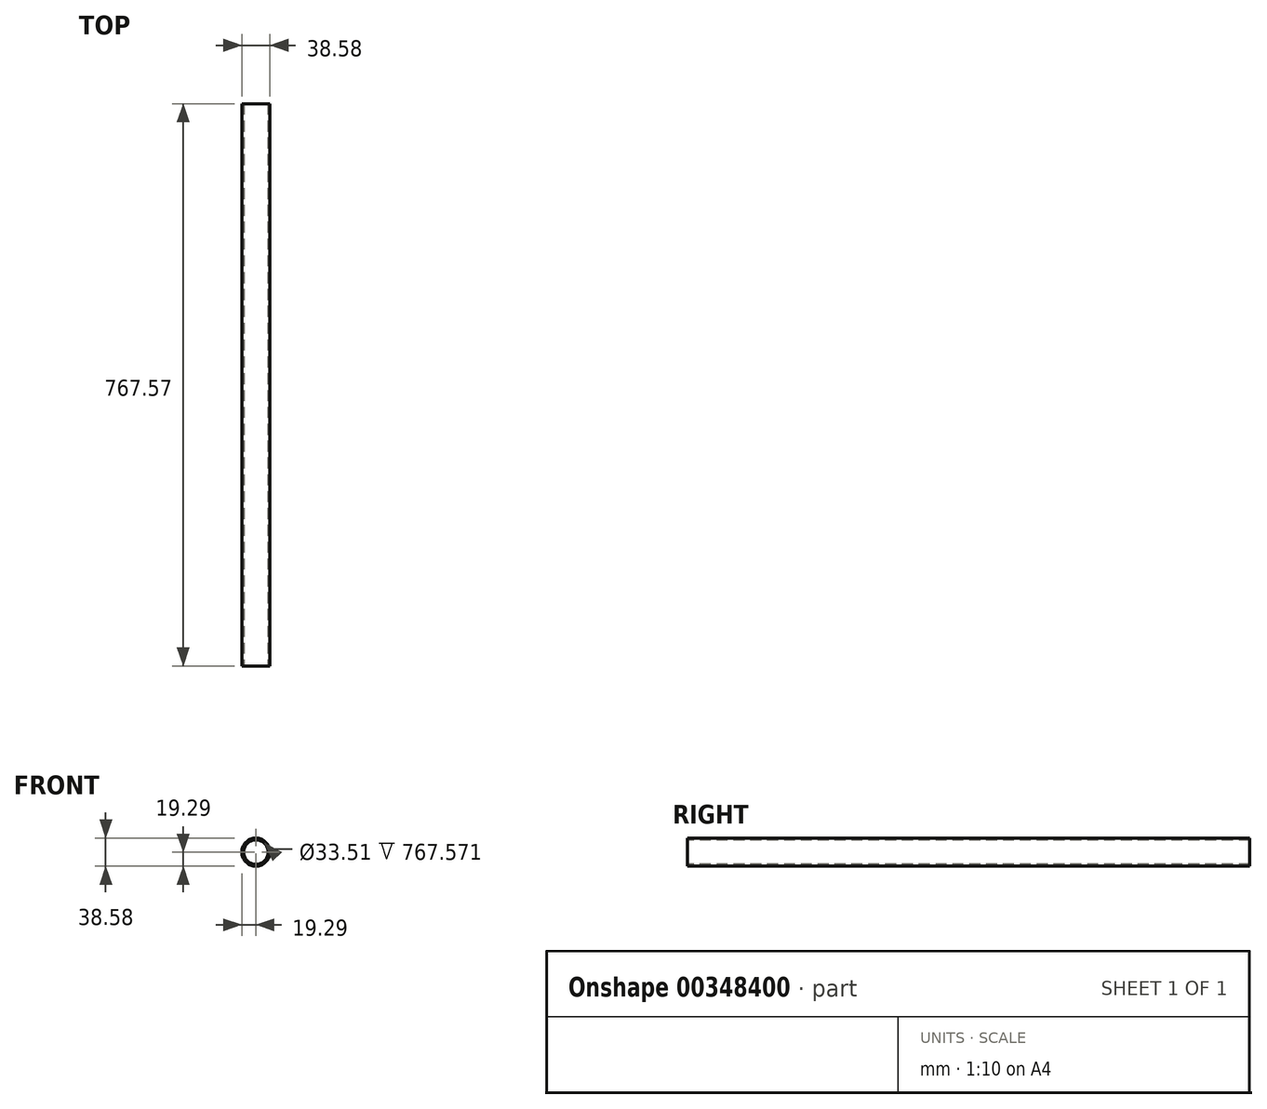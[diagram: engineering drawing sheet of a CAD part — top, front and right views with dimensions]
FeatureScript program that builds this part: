
annotation { "Feature Type Name" : "Feature", "Feature Type Description" : "" }
export const myFeature = defineFeature(function(context is Context, id is Id, definition is map)
    precondition{}
    {
        {
            var Q0;
            Q0=qCreatedBy(makeId("Front.planeOp"),FACE);
            var sketch = newSketch(context, id + "F0", { "sketchPlane" : qUnion([Q0])});
            skCircle(sketch, "E0", {"center": v(0, 0) * mm, "radius": 19.3 * mm});
            skSolve(sketch);
        }
        {
            var Q0;
            Q0=qCreatedBy(makeId("Top.planeOp"),FACE);
            var sketch = newSketch(context, id + "F1", { "sketchPlane" : qUnion([Q0])});
            skLineSegment(sketch, "E1", {"start": v(0, 0) * mm, "end": v(0, -767.57) * mm});
            skSolve(sketch);
        }
        {
            var Q0;
            Q0=makeQuery(id+"F0.imprint","IMPRINT",FACE,{"disambiguationData":[TD([[makeQuery(id+"F0.imprint","IMPRINT",EDGE,{"derivedFrom":sQuery(id+"F0.wireOp",EDGE,"E0")}),1.0]])]});
            var Q1;
            Q1=sQuery(id+"F1.wireOp",EDGE,"E1");
            sweep(context, id + "F2", {"profiles" : qUnion([Q0]), "path" : qUnion([Q1])});
        }
        {
            var Q0;
            Q0=makeQuery(id+"F2.opSweep","CAP_FACE",FACE,{"disambiguationData":[OSD([sQuery(id+"F0.wireOp",EDGE,"E0"),sQuery(id+"F1.wireOp",VERTEX,"E1.end")])],"isStart":false});
            var Q1;
            Q1=makeQuery(id+"F2.opSweep","CAP_FACE",FACE,{"disambiguationData":[OSD([sQuery(id+"F0.wireOp",EDGE,"E0"),sQuery(id+"F1.wireOp",VERTEX,"E1.start")])],"isStart":true});
            shell(context, id + "F3", {"entities" : qUnion([Q0, Q1]), "thickness" : 2.54 * mm});
        }
    });
